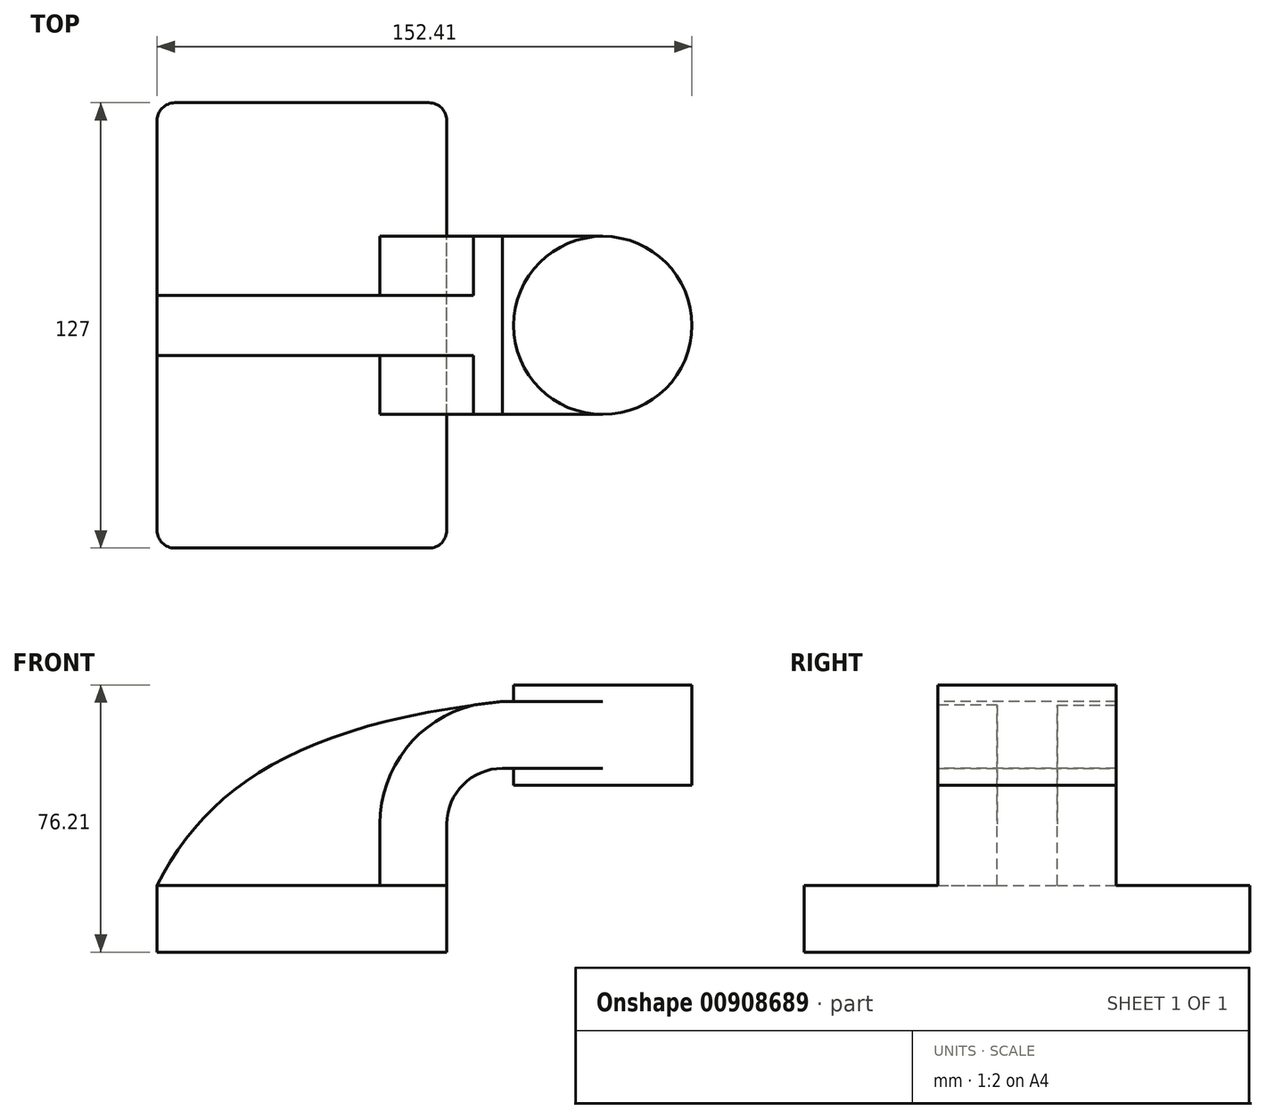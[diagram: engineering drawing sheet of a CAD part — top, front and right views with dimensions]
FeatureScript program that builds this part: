
annotation { "Feature Type Name" : "Feature", "Feature Type Description" : "" }
export const myFeature = defineFeature(function(context is Context, id is Id, definition is map)
    precondition{}
    {
        {
            var Q0;
            Q0=qCreatedBy(makeId("Front.planeOp"),FACE);
            var sketch = newSketch(context, id + "F0", { "sketchPlane" : qUnion([Q0])});
            skLineSegment(sketch, "E0.bottom", {"start": v(41.28, -9.52) * mm, "end": v(-41.28, -9.53) * mm});
            skLineSegment(sketch, "E0.top", {"start": v(41.28, 9.53) * mm, "end": v(-41.28, 9.53) * mm});
            skLineSegment(sketch, "E0.left", {"start": v(41.28, -9.52) * mm, "end": v(41.28, 9.53) * mm});
            skLineSegment(sketch, "E0.right", {"start": v(-41.28, -9.53) * mm, "end": v(-41.28, 9.53) * mm});
            skPoint(sketch, "E0.middle", {"position": v(0, 0) * mm});
            skLineSegment(sketch, "E1.bottom", {"start": v(60.32, 66.68) * mm, "end": v(111.12, 66.68) * mm});
            skLineSegment(sketch, "E1.top", {"start": v(60.32, 38.1) * mm, "end": v(111.12, 38.1) * mm});
            skLineSegment(sketch, "E1.left", {"start": v(60.32, 66.68) * mm, "end": v(60.32, 38.1) * mm});
            skLineSegment(sketch, "E1.right", {"start": v(111.12, 66.68) * mm, "end": v(111.12, 38.1) * mm});
            skLineSegment(sketch, "E2", {"start": v(41.28, 9.53) * mm, "end": v(41.28, 27) * mm});
            skArc(sketch, "E3", {"start": v(41.28, 27) * mm, "mid": v(45.92, 38.23) * mm, "end": v(57.15, 42.88) * mm});
            skLineSegment(sketch, "E4", {"start": v(57.15, 42.88) * mm, "end": v(85.72, 42.88) * mm});
            skLineSegment(sketch, "E5", {"start": v(85.72, 66.68) * mm, "end": v(85.72, 38.1) * mm});
            skArc(sketch, "E6.1", {"start": v(22.23, 27) * mm, "mid": v(32.45, 51.7) * mm, "end": v(57.15, 61.93) * mm});
            skLineSegment(sketch, "E6.2", {"start": v(22.23, 9.53) * mm, "end": v(22.23, 27) * mm});
            skLineSegment(sketch, "E7", {"start": v(57.15, 61.93) * mm, "end": v(85.72, 61.93) * mm});
            skFitSpline(sketch, "E8", {"points": [v(-41.28, 9.53) * mm, v(57.15, 61.93) * mm], "startDerivative": vector(42.67, 85.34) * mm, "endDerivative": vector(171.45, 18.52) * mm});
            skSolve(sketch);
        }
        {
            var Q0;
            Q0=makeQuery(id+"F0.imprint","IMPRINT",FACE,{"disambiguationData":[TD([[makeQuery(id+"F0.imprint","IMPRINT",EDGE,{"derivedFrom":sQuery(id+"F0.wireOp",EDGE,"E0.bottom")}),-1.0]])]});
            extrude(context, id + "F1", {"entities" : qUnion([Q0]), "depth" : 127 * mm, "offsetDistance" : 25.4 * mm, "symmetric" : true});
        }
        {
            var Q0;
            {var subQ1=sQuery(id+"F0.wireOp",EDGE,"E2");Q0=makeQuery(id+"F0.imprint","IMPRINT",FACE,{"disambiguationData":[TD([[makeQuery(id+"F0.imprint","IMPRINT",EDGE,{"derivedFrom":subQ1}),1.0]])]});}
            var Q1;
            {var subQ0=sQuery(id+"F0.wireOp",EDGE,"E7");var subQ1=sQuery(id+"F0.wireOp",EDGE,"E1.left");var subQ2=makeQuery(id+"F0.imprint","INTERSECT",VERTEX,{"derivedFrom":[subQ1,subQ0]});Q1=makeQuery(id+"F0.imprint","IMPRINT",FACE,{"disambiguationData":[TD([[makeQuery(id+"F0.imprint","IMPRINT",EDGE,{"disambiguationData":[TD([[subQ2,-1.0]])],"derivedFrom":subQ1}),1.0]])]});}
            extrude(context, id + "F2", {"entities" : qUnion([Q0, Q1]), "operationType" : NewBodyOperationType.ADD, "depth" : 50.8 * mm, "offsetDistance" : 25.4 * mm, "symmetric" : true});
        }
        {
            var Q0;
            {var subQ3=sQuery(id+"F0.wireOp",EDGE,"E6.2");Q0=makeQuery(id+"F0.imprint","IMPRINT",FACE,{"disambiguationData":[TD([[makeQuery(id+"F0.imprint","IMPRINT",EDGE,{"derivedFrom":subQ3}),1.0]])]});}
            extrude(context, id + "F3", {"entities" : qUnion([Q0]), "operationType" : NewBodyOperationType.ADD, "depth" : 17.14 * mm, "offsetDistance" : 25.4 * mm, "symmetric" : true});
        }
        {
            var Q0;
            {var subQ4=sQuery(id+"F0.wireOp",EDGE,"E1.right");Q0=makeQuery(id+"F0.imprint","IMPRINT",FACE,{"disambiguationData":[TD([[makeQuery(id+"F0.imprint","IMPRINT",EDGE,{"derivedFrom":subQ4}),-1.0]])]});}
            var Q1;
            Q1=sQuery(id+"F0.wireOp",EDGE,"E5");
            revolve(context, id + "F4", {"operationType" : NewBodyOperationType.ADD, "surfaceOperationType" : NewSurfaceOperationType.NEW, "entities" : qUnion([Q0]), "axis" : qUnion([Q1]), "revolveType" : RevolveType.FULL});
        }
        {
            var Q0;
            Q0=makeQuery(id+"F1.opExtrude","CAP_EDGE",EDGE,{"disambiguationData":[OSD([sQuery(id+"F0.wireOp",EDGE,"E0.left")])],"isStart":false});
            var Q1;
            Q1=makeQuery(id+"F1.opExtrude","CAP_EDGE",EDGE,{"disambiguationData":[OSD([sQuery(id+"F0.wireOp",EDGE,"E0.right")])],"isStart":false});
            fillet(context, id + "F5", {"entities" : qUnion([Q0, Q1]), "radius" : 5.08 * mm, "tangentPropagation" : true, "allowEdgeOverflow" : false});
        }
        {
            var Q0;
            Q0=makeQuery(id+"F1.opExtrude","CAP_EDGE",EDGE,{"disambiguationData":[OSD([sQuery(id+"F0.wireOp",EDGE,"E0.left")])],"isStart":true});
            var Q1;
            Q1=makeQuery(id+"F1.opExtrude","CAP_EDGE",EDGE,{"disambiguationData":[OSD([sQuery(id+"F0.wireOp",EDGE,"E0.right")])],"isStart":true});
            fillet(context, id + "F6", {"entities" : qUnion([Q0, Q1]), "radius" : 5.08 * mm, "tangentPropagation" : true, "allowEdgeOverflow" : false});
        }
    });
